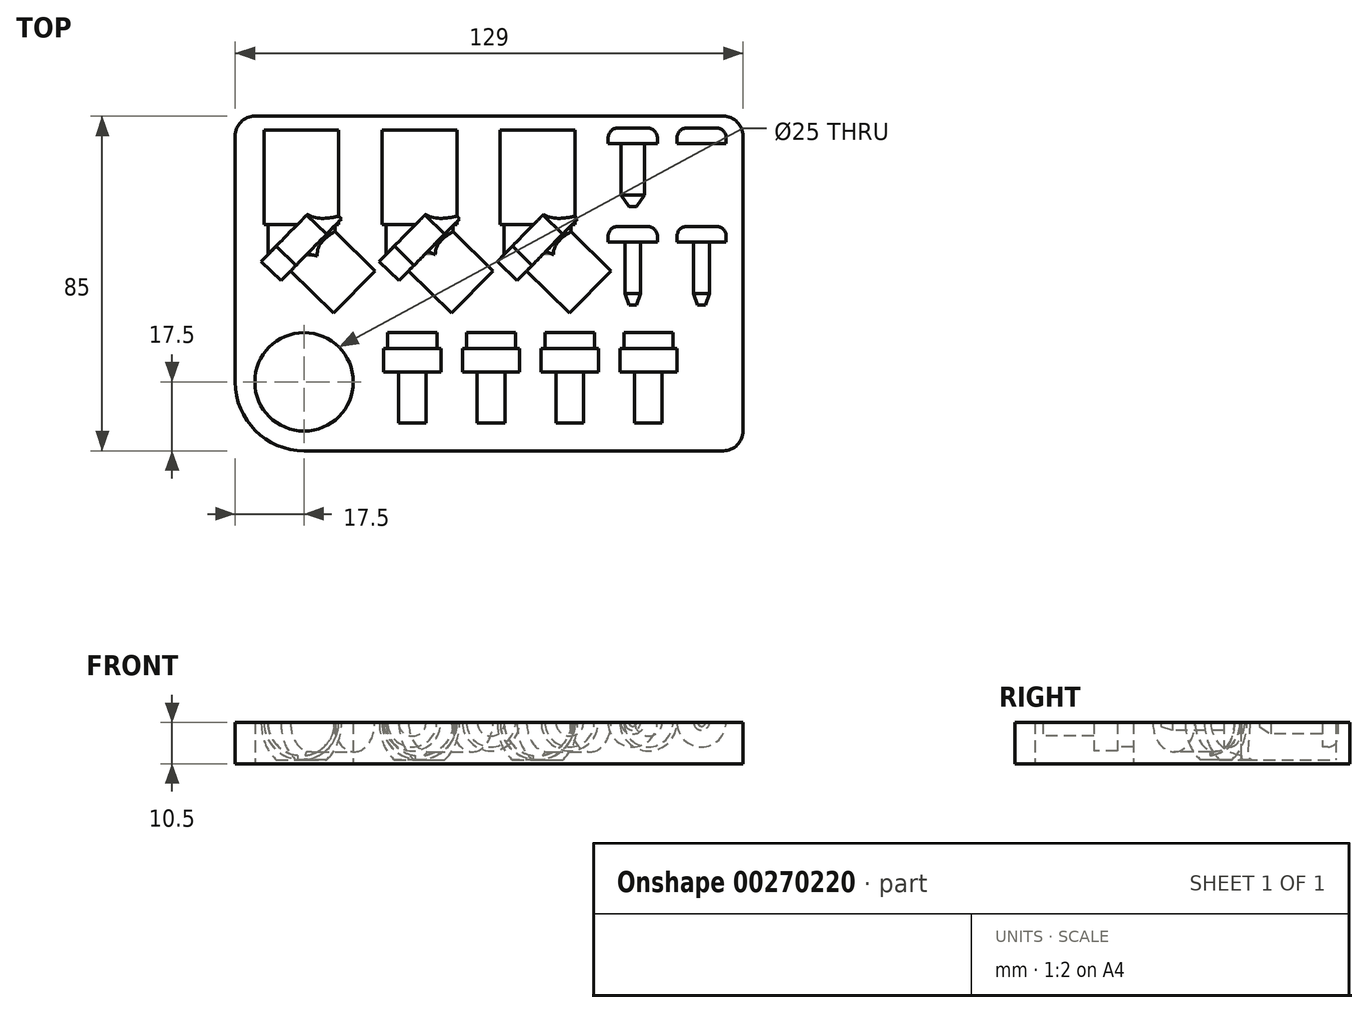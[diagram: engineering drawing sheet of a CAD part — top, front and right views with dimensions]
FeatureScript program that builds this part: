
annotation { "Feature Type Name" : "Feature", "Feature Type Description" : "" }
export const myFeature = defineFeature(function(context is Context, id is Id, definition is map)
    precondition{}
    {
        {
            var Q0;
            Q0=qCreatedBy(makeId("Top.planeOp"),FACE);
            var sketch = newSketch(context, id + "F0", { "sketchPlane" : qUnion([Q0])});
            skLineSegment(sketch, "E0.bottom", {"start": v(17.5, 0) * mm, "end": v(124, 0) * mm});
            skLineSegment(sketch, "E0.top", {"start": v(5, 85) * mm, "end": v(124, 85) * mm});
            skLineSegment(sketch, "E0.left", {"start": v(0, 17.5) * mm, "end": v(0, 80) * mm});
            skLineSegment(sketch, "E0.right", {"start": v(129, 5) * mm, "end": v(129, 80) * mm});
            skLineSegment(sketch, "E1.bottom", {"start": v(17.5, 0) * mm, "end": v(17.5, 0) * mm});
            skLineSegment(sketch, "E1.top", {"start": v(0, 17.5) * mm, "end": v(17.5, 17.5) * mm, "construction": true});
            skLineSegment(sketch, "E1.left", {"start": v(0, 17.5) * mm, "end": v(0, 17.5) * mm});
            skLineSegment(sketch, "E1.right", {"start": v(17.5, 0) * mm, "end": v(17.5, 17.5) * mm, "construction": true});
            skCircle(sketch, "E2", {"center": v(17.5, 17.5) * mm, "radius": 12.5 * mm});
            skPoint(sketch, "E3.visualSharp", {"position": v(0, 0) * mm});
            skArc(sketch, "E3.filletArc", {"start": v(0, 17.5) * mm, "mid": v(5.13, 5.13) * mm, "end": v(17.5, 0) * mm});
            skPoint(sketch, "E4.visualSharp", {"position": v(0, 85) * mm});
            skArc(sketch, "E4.filletArc", {"start": v(5, 85) * mm, "mid": v(1.46, 83.54) * mm, "end": v(0, 80) * mm});
            skPoint(sketch, "E5.visualSharp", {"position": v(129, 85) * mm});
            skArc(sketch, "E5.filletArc", {"start": v(129, 80) * mm, "mid": v(127.54, 83.54) * mm, "end": v(124, 85) * mm});
            skPoint(sketch, "E6.visualSharp", {"position": v(129, 0) * mm});
            skArc(sketch, "E6.filletArc", {"start": v(124, 0) * mm, "mid": v(127.54, 1.46) * mm, "end": v(129, 5) * mm});
            skSolve(sketch);
        }
        {
            var Q0;
            Q0=makeQuery(id+"F0.imprint","IMPRINT",FACE,{"disambiguationData":[TD([[makeQuery(id+"F0.imprint","IMPRINT",EDGE,{"derivedFrom":sQuery(id+"F0.wireOp",EDGE,"E0.bottom")}),1.0]])]});
            extrude(context, id + "F1", {"entities" : qUnion([Q0]), "depth" : 10.5 * mm});
        }
        {
            var Q0;
            Q0=makeQuery(id+"F1.opExtrude","CAP_FACE",FACE,{"disambiguationData":[OSD([sQuery(id+"F0.wireOp",EDGE,"E0.bottom"),sQuery(id+"F0.wireOp",EDGE,"E0.top"),sQuery(id+"F0.wireOp",EDGE,"E0.left"),sQuery(id+"F0.wireOp",EDGE,"E0.right"),sQuery(id+"F0.wireOp",EDGE,"E2"),sQuery(id+"F0.wireOp",EDGE,"E3.filletArc"),sQuery(id+"F0.wireOp",EDGE,"E4.filletArc"),sQuery(id+"F0.wireOp",EDGE,"E5.filletArc"),sQuery(id+"F0.wireOp",EDGE,"E6.filletArc")])],"isStart":false});
            var sketch = newSketch(context, id + "F2", { "sketchPlane" : qUnion([Q0])});
            skLineSegment(sketch, "E7.bottom", {"start": v(0, 0) * mm, "end": v(25, 0) * mm, "construction": true});
            skLineSegment(sketch, "E7.top", {"start": v(0, 35) * mm, "end": v(25, 35) * mm, "construction": true});
            skLineSegment(sketch, "E7.left", {"start": v(0, 0) * mm, "end": v(0, 35) * mm, "construction": true});
            skLineSegment(sketch, "E7.right", {"start": v(25, 0) * mm, "end": v(25, 35) * mm, "construction": true});
            skLineSegment(sketch, "E8", {"start": v(25, 35) * mm, "end": v(14.07, 45.7) * mm});
            skLineSegment(sketch, "E9", {"start": v(14.07, 45.7) * mm, "end": v(11.62, 43.2) * mm});
            skLineSegment(sketch, "E10", {"start": v(11.62, 43.2) * mm, "end": v(6.62, 48.1) * mm});
            skLineSegment(sketch, "E11", {"start": v(6.62, 48.1) * mm, "end": v(14.32, 55.96) * mm});
            skLineSegment(sketch, "E12", {"start": v(14.32, 55.96) * mm, "end": v(30.25, 40.36) * mm});
            skLineSegment(sketch, "E13", {"start": v(25, 35) * mm, "end": v(30.25, 40.36) * mm});
            skLineSegment(sketch, "E14", {"start": v(14.32, 55.96) * mm, "end": v(16.82, 53.51) * mm, "construction": true});
            skLineSegment(sketch, "E15", {"start": v(16.82, 53.51) * mm, "end": v(16.82, 81.51) * mm});
            skLineSegment(sketch, "E16", {"start": v(16.82, 81.51) * mm, "end": v(7.32, 81.51) * mm});
            skLineSegment(sketch, "E17", {"start": v(7.32, 81.51) * mm, "end": v(7.32, 57.51) * mm});
            skLineSegment(sketch, "E18", {"start": v(7.32, 57.51) * mm, "end": v(8.32, 57.51) * mm});
            skLineSegment(sketch, "E19", {"start": v(8.32, 57.51) * mm, "end": v(8.32, 53.16) * mm});
            skLineSegment(sketch, "E20", {"start": v(46.82, 53.51) * mm, "end": v(46.82, 81.51) * mm});
            skLineSegment(sketch, "E21", {"start": v(46.82, 81.51) * mm, "end": v(37.32, 81.51) * mm});
            skLineSegment(sketch, "E22", {"start": v(37.32, 81.51) * mm, "end": v(37.32, 57.51) * mm});
            skLineSegment(sketch, "E23", {"start": v(37.32, 57.51) * mm, "end": v(38.32, 57.51) * mm});
            skLineSegment(sketch, "E24", {"start": v(76.82, 53.51) * mm, "end": v(76.82, 81.51) * mm});
            skLineSegment(sketch, "E25", {"start": v(76.82, 81.51) * mm, "end": v(67.32, 81.51) * mm});
            skLineSegment(sketch, "E26", {"start": v(67.32, 81.51) * mm, "end": v(67.32, 57.51) * mm});
            skLineSegment(sketch, "E27", {"start": v(67.32, 57.51) * mm, "end": v(68.32, 57.51) * mm});
            skLineSegment(sketch, "E28", {"start": v(8.32, 57.51) * mm, "end": v(8.32, 49.51) * mm});
            skLineSegment(sketch, "E29", {"start": v(8.32, 49.51) * mm, "end": v(16.82, 53.51) * mm});
            skLineSegment(sketch, "E30", {"start": v(38.32, 57.51) * mm, "end": v(38.32, 49.51) * mm});
            skLineSegment(sketch, "E31", {"start": v(38.32, 49.51) * mm, "end": v(46.82, 53.51) * mm});
            skLineSegment(sketch, "E32", {"start": v(68.32, 57.51) * mm, "end": v(68.32, 49.51) * mm});
            skLineSegment(sketch, "E33", {"start": v(68.32, 49.51) * mm, "end": v(76.82, 53.51) * mm});
            skLineSegment(sketch, "E34", {"start": v(46.82, 53.51) * mm, "end": v(44.32, 55.96) * mm});
            skLineSegment(sketch, "E35", {"start": v(44.32, 55.96) * mm, "end": v(36.62, 48.1) * mm});
            skLineSegment(sketch, "E36", {"start": v(36.62, 48.1) * mm, "end": v(41.62, 43.2) * mm});
            skLineSegment(sketch, "E37", {"start": v(41.62, 43.2) * mm, "end": v(44.07, 45.7) * mm});
            skLineSegment(sketch, "E38", {"start": v(44.07, 45.7) * mm, "end": v(55, 35) * mm});
            skLineSegment(sketch, "E39", {"start": v(55, 35) * mm, "end": v(60.25, 40.36) * mm});
            skLineSegment(sketch, "E40", {"start": v(46.82, 53.51) * mm, "end": v(60.25, 40.36) * mm});
            skLineSegment(sketch, "E41", {"start": v(76.82, 53.51) * mm, "end": v(74.32, 55.96) * mm});
            skLineSegment(sketch, "E42", {"start": v(74.32, 55.96) * mm, "end": v(66.62, 48.1) * mm});
            skLineSegment(sketch, "E43", {"start": v(66.62, 48.1) * mm, "end": v(71.62, 43.2) * mm});
            skLineSegment(sketch, "E44", {"start": v(71.62, 43.2) * mm, "end": v(74.07, 45.7) * mm});
            skLineSegment(sketch, "E45", {"start": v(74.07, 45.7) * mm, "end": v(85, 35) * mm});
            skLineSegment(sketch, "E46", {"start": v(76.82, 53.51) * mm, "end": v(90.25, 40.36) * mm});
            skLineSegment(sketch, "E47", {"start": v(85, 35) * mm, "end": v(90.25, 40.36) * mm});
            skLineSegment(sketch, "E48", {"start": v(16.82, 53.51) * mm, "end": v(46.82, 53.51) * mm, "construction": true});
            skLineSegment(sketch, "E49", {"start": v(46.82, 53.51) * mm, "end": v(76.82, 53.51) * mm, "construction": true});
            skSolve(sketch);
        }
        {
            var Q0;
            {var subQ0=sQuery(id+"F2.wireOp",EDGE,"E15");Q0=makeQuery(id+"F2.imprint","IMPRINT",FACE,{"disambiguationData":[TD([[makeQuery(id+"F2.imprint","IMPRINT",EDGE,{"derivedFrom":subQ0}),1.0]])]});}
            var Q1;
            {var subQ5=sQuery(id+"F2.wireOp",EDGE,"E29");Q1=makeQuery(id+"F2.imprint","IMPRINT",FACE,{"disambiguationData":[TD([[makeQuery(id+"F2.imprint","IMPRINT",EDGE,{"derivedFrom":subQ5}),1.0]])]});}
            var Q2;
            Q2=sQuery(id+"F2.wireOp",EDGE,"E15");
            revolve(context, id + "F3", {"operationType" : NewBodyOperationType.REMOVE, "entities" : qUnion([Q0, Q1]), "axis" : qUnion([Q2]), "revolveType" : RevolveType.FULL, "oppositeDirection" : true});
        }
        {
            var Q0;
            Q0=makeQuery(id+"F2.imprint","IMPRINT",FACE,{"disambiguationData":[TD([[makeQuery(id+"F2.imprint","IMPRINT",EDGE,{"derivedFrom":sQuery(id+"F2.wireOp",EDGE,"E20")}),1.0]])]});
            var Q1;
            Q1=sQuery(id+"F2.wireOp",EDGE,"E20");
            revolve(context, id + "F4", {"operationType" : NewBodyOperationType.REMOVE, "entities" : qUnion([Q0]), "axis" : qUnion([Q1]), "revolveType" : RevolveType.FULL, "oppositeDirection" : true});
        }
        {
            var Q0;
            Q0=makeQuery(id+"F2.imprint","IMPRINT",FACE,{"disambiguationData":[TD([[makeQuery(id+"F2.imprint","IMPRINT",EDGE,{"derivedFrom":sQuery(id+"F2.wireOp",EDGE,"E24")}),1.0]])]});
            var Q1;
            Q1=sQuery(id+"F2.wireOp",EDGE,"E24");
            revolve(context, id + "F5", {"operationType" : NewBodyOperationType.REMOVE, "entities" : qUnion([Q0]), "axis" : qUnion([Q1]), "revolveType" : RevolveType.FULL, "oppositeDirection" : true});
        }
        {
            var Q0;
            Q0=makeQuery(id+"F2.imprint","IMPRINT",FACE,{"disambiguationData":[TD([[makeQuery(id+"F2.imprint","IMPRINT",EDGE,{"derivedFrom":sQuery(id+"F2.wireOp",EDGE,"E8")}),-1.0]])]});
            var Q1;
            {var subQ5=sQuery(id+"F2.wireOp",EDGE,"E29");Q1=makeQuery(id+"F2.imprint","IMPRINT",FACE,{"disambiguationData":[TD([[makeQuery(id+"F2.imprint","IMPRINT",EDGE,{"derivedFrom":subQ5}),1.0]])]});}
            var Q2;
            Q2=sQuery(id+"F2.wireOp",EDGE,"E12");
            revolve(context, id + "F6", {"operationType" : NewBodyOperationType.REMOVE, "entities" : qUnion([Q0, Q1]), "axis" : qUnion([Q2]), "revolveType" : RevolveType.FULL, "oppositeDirection" : true});
        }
        {
            var Q0;
            {var subQ4=sQuery(id+"F2.wireOp",EDGE,"E31");Q0=makeQuery(id+"F2.imprint","IMPRINT",FACE,{"disambiguationData":[TD([[makeQuery(id+"F2.imprint","IMPRINT",EDGE,{"derivedFrom":subQ4}),-1.0]])]});}
            var Q1;
            {var subQ0=sQuery(id+"F2.wireOp",EDGE,"E31");Q1=makeQuery(id+"F2.imprint","IMPRINT",FACE,{"disambiguationData":[TD([[makeQuery(id+"F2.imprint","IMPRINT",EDGE,{"derivedFrom":subQ0}),1.0]])]});}
            var Q2;
            Q2=sQuery(id+"F2.wireOp",EDGE,"E40");
            revolve(context, id + "F7", {"operationType" : NewBodyOperationType.REMOVE, "entities" : qUnion([Q0, Q1]), "axis" : qUnion([Q2]), "revolveType" : RevolveType.FULL, "oppositeDirection" : true});
        }
        {
            var Q0;
            {var subQ4=sQuery(id+"F2.wireOp",EDGE,"E33");Q0=makeQuery(id+"F2.imprint","IMPRINT",FACE,{"disambiguationData":[TD([[makeQuery(id+"F2.imprint","IMPRINT",EDGE,{"derivedFrom":subQ4}),-1.0]])]});}
            var Q1;
            {var subQ0=sQuery(id+"F2.wireOp",EDGE,"E33");Q1=makeQuery(id+"F2.imprint","IMPRINT",FACE,{"disambiguationData":[TD([[makeQuery(id+"F2.imprint","IMPRINT",EDGE,{"derivedFrom":subQ0}),1.0]])]});}
            var Q2;
            Q2=sQuery(id+"F2.wireOp",EDGE,"E46");
            revolve(context, id + "F8", {"operationType" : NewBodyOperationType.REMOVE, "entities" : qUnion([Q0, Q1]), "axis" : qUnion([Q2]), "revolveType" : RevolveType.FULL, "oppositeDirection" : true});
        }
        {
            var Q0;
            Q0=makeQuery(id+"F1.opExtrude","CAP_FACE",FACE,{"disambiguationData":[OSD([sQuery(id+"F0.wireOp",EDGE,"E0.bottom"),sQuery(id+"F0.wireOp",EDGE,"E0.top"),sQuery(id+"F0.wireOp",EDGE,"E0.left"),sQuery(id+"F0.wireOp",EDGE,"E0.right"),sQuery(id+"F0.wireOp",EDGE,"E2"),sQuery(id+"F0.wireOp",EDGE,"E3.filletArc"),sQuery(id+"F0.wireOp",EDGE,"E4.filletArc"),sQuery(id+"F0.wireOp",EDGE,"E5.filletArc"),sQuery(id+"F0.wireOp",EDGE,"E6.filletArc")])],"isStart":false});
            var sketch = newSketch(context, id + "F9", { "sketchPlane" : qUnion([Q0])});
            skLineSegment(sketch, "E50.0.0", {"start": v(124, 85) * mm, "end": v(5, 85) * mm});
            skArc(sketch, "E50.0.1", {"start": v(5, 85) * mm, "mid": v(1.46, 83.54) * mm, "end": v(0, 80) * mm});
            skLineSegment(sketch, "E50.0.2", {"start": v(0, 80) * mm, "end": v(0, 17.5) * mm});
            skArc(sketch, "E50.0.3", {"start": v(0, 17.5) * mm, "mid": v(5.13, 5.13) * mm, "end": v(17.5, 0) * mm});
            skLineSegment(sketch, "E50.0.4", {"start": v(17.5, 0) * mm, "end": v(124, 0) * mm});
            skArc(sketch, "E50.0.5", {"start": v(124, 0) * mm, "mid": v(127.54, 1.46) * mm, "end": v(129, 5) * mm});
            skLineSegment(sketch, "E50.0.6", {"start": v(129, 5) * mm, "end": v(129, 80) * mm});
            skArc(sketch, "E50.0.7", {"start": v(129, 80) * mm, "mid": v(127.54, 83.54) * mm, "end": v(124, 85) * mm});
            skCircle(sketch, "E51.0", {"center": v(17.5, 17.5) * mm, "radius": 12.5 * mm});
            skSolve(sketch);
        }
        {
            var Q0;
            Q0 = qSketchRegion(id + "F9", true);
            extrude(context, id + "F10", {"entities" : qUnion([Q0]), "operationType" : NewBodyOperationType.ADD, "oppositeDirection" : true, "depth" : 10.5 * mm, "hasSecondDirection" : true, "secondDirectionOppositeDirection" : true, "secondDirectionDepth" : 9.5 * mm});
        }
        {
            var Q0;
            Q0=makeQuery(id+"F1.opExtrude","CAP_FACE",FACE,{"disambiguationData":[OSD([sQuery(id+"F0.wireOp",EDGE,"E0.bottom"),sQuery(id+"F0.wireOp",EDGE,"E0.top"),sQuery(id+"F0.wireOp",EDGE,"E0.left"),sQuery(id+"F0.wireOp",EDGE,"E0.right"),sQuery(id+"F0.wireOp",EDGE,"E2"),sQuery(id+"F0.wireOp",EDGE,"E3.filletArc"),sQuery(id+"F0.wireOp",EDGE,"E4.filletArc"),sQuery(id+"F0.wireOp",EDGE,"E5.filletArc"),sQuery(id+"F0.wireOp",EDGE,"E6.filletArc")])],"isStart":false});
            var sketch = newSketch(context, id + "F11", { "sketchPlane" : qUnion([Q0])});
            skLineSegment(sketch, "E52.bottom", {"start": v(0, 0) * mm, "end": v(101, 0) * mm, "construction": true});
            skLineSegment(sketch, "E52.top", {"start": v(0, 82) * mm, "end": v(101, 82) * mm, "construction": true});
            skLineSegment(sketch, "E52.left", {"start": v(0, 0) * mm, "end": v(0, 82) * mm, "construction": true});
            skLineSegment(sketch, "E52.right", {"start": v(101, 0) * mm, "end": v(101, 82) * mm, "construction": true});
            skLineSegment(sketch, "E53.bottom", {"start": v(101, 82) * mm, "end": v(104.75, 82) * mm});
            skLineSegment(sketch, "E53.top", {"start": v(104, 78) * mm, "end": v(107.25, 78) * mm});
            skLineSegment(sketch, "E53.left", {"start": v(101, 82) * mm, "end": v(101, 78) * mm});
            skLineSegment(sketch, "E53.right", {"start": v(107.25, 79.5) * mm, "end": v(107.25, 78) * mm});
            skPoint(sketch, "E54.visualSharp", {"position": v(107.25, 82) * mm});
            skArc(sketch, "E54.filletArc", {"start": v(107.25, 79.5) * mm, "mid": v(106.52, 81.27) * mm, "end": v(104.75, 82) * mm});
            skLineSegment(sketch, "E55.left", {"start": v(101, 78) * mm, "end": v(101, 72) * mm});
            skLineSegment(sketch, "E55.right", {"start": v(104, 78) * mm, "end": v(104, 65) * mm});
            skLineSegment(sketch, "E56", {"start": v(101, 82) * mm, "end": v(118.5, 82) * mm, "construction": true});
            skLineSegment(sketch, "E57.bottom", {"start": v(118.5, 82) * mm, "end": v(122.25, 82) * mm});
            skLineSegment(sketch, "E57.top", {"start": v(118.5, 78) * mm, "end": v(124.75, 78) * mm});
            skLineSegment(sketch, "E57.left", {"start": v(118.5, 82) * mm, "end": v(118.5, 78) * mm});
            skLineSegment(sketch, "E57.right", {"start": v(124.75, 79.5) * mm, "end": v(124.75, 78) * mm});
            skLineSegment(sketch, "E58.bottom", {"start": v(118.5, 78) * mm, "end": v(121.5, 78) * mm});
            skLineSegment(sketch, "E58.top", {"start": v(118.5, 62) * mm, "end": v(119.5, 62) * mm});
            skLineSegment(sketch, "E58.left", {"start": v(118.5, 78) * mm, "end": v(118.5, 62) * mm});
            skLineSegment(sketch, "E58.right", {"start": v(121.5, 78) * mm, "end": v(121.5, 65) * mm});
            skPoint(sketch, "E59.visualSharp", {"position": v(124.75, 82) * mm});
            skArc(sketch, "E59.filletArc", {"start": v(124.75, 79.5) * mm, "mid": v(124.02, 81.27) * mm, "end": v(122.25, 82) * mm});
            skLineSegment(sketch, "E60", {"start": v(118.5, 62) * mm, "end": v(119.5, 62) * mm, "construction": true});
            skLineSegment(sketch, "E61", {"start": v(119.5, 62) * mm, "end": v(121.5, 65) * mm});
            skLineSegment(sketch, "E62", {"start": v(101, 78) * mm, "end": v(101, 62) * mm});
            skLineSegment(sketch, "E63", {"start": v(101, 62) * mm, "end": v(102, 62) * mm});
            skLineSegment(sketch, "E64", {"start": v(102, 62) * mm, "end": v(104, 65) * mm});
            skLineSegment(sketch, "E65", {"start": v(101, 62) * mm, "end": v(101, 57) * mm, "construction": true});
            skLineSegment(sketch, "E66.bottom", {"start": v(101, 57) * mm, "end": v(104.75, 57) * mm});
            skLineSegment(sketch, "E66.top", {"start": v(103, 53) * mm, "end": v(107.25, 53) * mm});
            skLineSegment(sketch, "E66.left", {"start": v(101, 57) * mm, "end": v(101, 53) * mm});
            skLineSegment(sketch, "E66.right", {"start": v(107.25, 54.5) * mm, "end": v(107.25, 53) * mm});
            skLineSegment(sketch, "E67.left", {"start": v(101, 53) * mm, "end": v(101, 37) * mm});
            skLineSegment(sketch, "E68", {"start": v(103, 53) * mm, "end": v(103, 40) * mm});
            skLineSegment(sketch, "E69", {"start": v(101, 37) * mm, "end": v(102, 37) * mm});
            skLineSegment(sketch, "E70", {"start": v(102, 37) * mm, "end": v(103, 40) * mm});
            skPoint(sketch, "E71.visualSharp", {"position": v(107.25, 57) * mm});
            skArc(sketch, "E71.filletArc", {"start": v(107.25, 54.5) * mm, "mid": v(106.52, 56.27) * mm, "end": v(104.75, 57) * mm});
            skLineSegment(sketch, "E72", {"start": v(101, 57) * mm, "end": v(118.5, 57) * mm, "construction": true});
            skLineSegment(sketch, "E73.bottom", {"start": v(118.5, 57) * mm, "end": v(122.25, 57) * mm});
            skLineSegment(sketch, "E73.top", {"start": v(120.5, 53) * mm, "end": v(124.75, 53) * mm});
            skLineSegment(sketch, "E73.left", {"start": v(118.5, 57) * mm, "end": v(118.5, 53) * mm});
            skLineSegment(sketch, "E73.right", {"start": v(124.75, 54.5) * mm, "end": v(124.75, 53) * mm});
            skLineSegment(sketch, "E74.left", {"start": v(118.5, 53) * mm, "end": v(118.5, 37) * mm});
            skLineSegment(sketch, "E75", {"start": v(120.5, 53) * mm, "end": v(120.5, 40) * mm});
            skLineSegment(sketch, "E76", {"start": v(118.5, 37) * mm, "end": v(119.5, 37) * mm});
            skLineSegment(sketch, "E77", {"start": v(119.5, 37) * mm, "end": v(120.5, 40) * mm});
            skPoint(sketch, "E78.visualSharp", {"position": v(124.75, 57) * mm});
            skArc(sketch, "E78.filletArc", {"start": v(124.75, 54.5) * mm, "mid": v(124.02, 56.27) * mm, "end": v(122.25, 57) * mm});
            skSolve(sketch);
        }
        {
            var Q0;
            Q0=makeQuery(id+"F11.imprint","IMPRINT",FACE,{"disambiguationData":[TD([[makeQuery(id+"F11.imprint","IMPRINT",EDGE,{"derivedFrom":sQuery(id+"F11.wireOp",EDGE,"E53.bottom")}),-1.0]])]});
            var Q1;
            Q1=makeQuery(id+"F11.imprint","IMPRINT",FACE,{"disambiguationData":[TD([[makeQuery(id+"F11.imprint","IMPRINT",EDGE,{"derivedFrom":sQuery(id+"F11.wireOp",EDGE,"E66.bottom")}),-1.0]])]});
            var Q2;
            Q2=sQuery(id+"F11.wireOp",EDGE,"E67.left");
            revolve(context, id + "F12", {"operationType" : NewBodyOperationType.REMOVE, "entities" : qUnion([Q0, Q1]), "axis" : qUnion([Q2]), "revolveType" : RevolveType.FULL, "oppositeDirection" : true});
        }
        {
            var Q0;
            Q0=makeQuery(id+"F11.imprint","IMPRINT",FACE,{"disambiguationData":[TD([[makeQuery(id+"F11.imprint","IMPRINT",EDGE,{"derivedFrom":sQuery(id+"F11.wireOp",EDGE,"E58.bottom")}),-1.0]])]});
            var Q1;
            Q1=makeQuery(id+"F11.imprint","IMPRINT",FACE,{"disambiguationData":[TD([[makeQuery(id+"F11.imprint","IMPRINT",EDGE,{"derivedFrom":sQuery(id+"F11.wireOp",EDGE,"E57.bottom")}),-1.0]])]});
            var Q2;
            Q2=makeQuery(id+"F11.imprint","IMPRINT",FACE,{"disambiguationData":[TD([[makeQuery(id+"F11.imprint","IMPRINT",EDGE,{"derivedFrom":sQuery(id+"F11.wireOp",EDGE,"E73.bottom")}),-1.0]])]});
            var Q3;
            Q3=sQuery(id+"F11.wireOp",EDGE,"E74.left");
            revolve(context, id + "F13", {"operationType" : NewBodyOperationType.REMOVE, "entities" : qUnion([Q0, Q1, Q2]), "axis" : qUnion([Q3]), "revolveType" : RevolveType.FULL, "oppositeDirection" : true});
        }
        {
            var Q0;
            Q0=makeQuery(id+"F1.opExtrude","CAP_FACE",FACE,{"disambiguationData":[OSD([sQuery(id+"F0.wireOp",EDGE,"E0.bottom"),sQuery(id+"F0.wireOp",EDGE,"E0.top"),sQuery(id+"F0.wireOp",EDGE,"E0.left"),sQuery(id+"F0.wireOp",EDGE,"E0.right"),sQuery(id+"F0.wireOp",EDGE,"E2"),sQuery(id+"F0.wireOp",EDGE,"E3.filletArc"),sQuery(id+"F0.wireOp",EDGE,"E4.filletArc"),sQuery(id+"F0.wireOp",EDGE,"E5.filletArc"),sQuery(id+"F0.wireOp",EDGE,"E6.filletArc")])],"isStart":false});
            var sketch = newSketch(context, id + "F14", { "sketchPlane" : qUnion([Q0])});
            skLineSegment(sketch, "E79.bottom", {"start": v(0, 0) * mm, "end": v(45, 0) * mm, "construction": true});
            skLineSegment(sketch, "E79.top", {"start": v(0, 30) * mm, "end": v(45, 30) * mm, "construction": true});
            skLineSegment(sketch, "E79.left", {"start": v(0, 0) * mm, "end": v(0, 30) * mm, "construction": true});
            skLineSegment(sketch, "E79.right", {"start": v(45, 0) * mm, "end": v(45, 17.5) * mm, "construction": true});
            skLineSegment(sketch, "E80.bottom", {"start": v(45, 30) * mm, "end": v(51.25, 30) * mm});
            skLineSegment(sketch, "E80.left", {"start": v(45, 30) * mm, "end": v(45, 26) * mm});
            skLineSegment(sketch, "E80.right", {"start": v(51.25, 30) * mm, "end": v(51.25, 26) * mm});
            skLineSegment(sketch, "E81.bottom", {"start": v(51.25, 26) * mm, "end": v(52.25, 26) * mm});
            skLineSegment(sketch, "E81.left", {"start": v(45, 26) * mm, "end": v(45, 17.5) * mm});
            skPoint(sketch, "E81.right.end.orphan", {"position": v(47.25, 17.5) * mm});
            skLineSegment(sketch, "E82.trimOffspring", {"start": v(45, 26) * mm, "end": v(45, 30) * mm, "construction": true});
            skLineSegment(sketch, "E83", {"start": v(52.25, 26) * mm, "end": v(52.25, 20) * mm});
            skLineSegment(sketch, "E84", {"start": v(52.25, 20) * mm, "end": v(48.5, 20) * mm});
            skLineSegment(sketch, "E85", {"start": v(45, 20) * mm, "end": v(45, 26) * mm});
            skLineSegment(sketch, "E86.top", {"start": v(45, 7) * mm, "end": v(48.5, 7) * mm});
            skLineSegment(sketch, "E86.left", {"start": v(45, 20) * mm, "end": v(45, 7) * mm});
            skLineSegment(sketch, "E86.right", {"start": v(48.5, 20) * mm, "end": v(48.5, 7) * mm});
            skLineSegment(sketch, "E87", {"start": v(45, 30) * mm, "end": v(65, 30) * mm, "construction": true});
            skLineSegment(sketch, "E88", {"start": v(65, 30) * mm, "end": v(85, 30) * mm, "construction": true});
            skLineSegment(sketch, "E89", {"start": v(85, 30) * mm, "end": v(105, 30) * mm, "construction": true});
            skLineSegment(sketch, "E90.bottom", {"start": v(65, 30) * mm, "end": v(71.25, 30) * mm});
            skLineSegment(sketch, "E90.left", {"start": v(65, 30) * mm, "end": v(65, 26) * mm});
            skLineSegment(sketch, "E90.right", {"start": v(71.25, 30) * mm, "end": v(71.25, 26) * mm});
            skLineSegment(sketch, "E91.bottom", {"start": v(85, 30) * mm, "end": v(91.25, 30) * mm});
            skLineSegment(sketch, "E91.left", {"start": v(85, 30) * mm, "end": v(85, 26) * mm});
            skLineSegment(sketch, "E91.right", {"start": v(91.25, 30) * mm, "end": v(91.25, 26) * mm});
            skLineSegment(sketch, "E92.bottom", {"start": v(105, 30) * mm, "end": v(111.25, 30) * mm});
            skLineSegment(sketch, "E92.left", {"start": v(105, 30) * mm, "end": v(105, 26) * mm});
            skLineSegment(sketch, "E92.right", {"start": v(111.25, 30) * mm, "end": v(111.25, 26) * mm});
            skLineSegment(sketch, "E93.bottom", {"start": v(71.25, 26) * mm, "end": v(72.25, 26) * mm});
            skLineSegment(sketch, "E93.top", {"start": v(68.5, 20) * mm, "end": v(72.25, 20) * mm});
            skLineSegment(sketch, "E93.left", {"start": v(65, 26) * mm, "end": v(65, 20) * mm});
            skLineSegment(sketch, "E93.right", {"start": v(72.25, 26) * mm, "end": v(72.25, 20) * mm});
            skLineSegment(sketch, "E94.bottom", {"start": v(91.25, 26) * mm, "end": v(92.25, 26) * mm});
            skLineSegment(sketch, "E94.top", {"start": v(88.5, 20) * mm, "end": v(92.25, 20) * mm});
            skLineSegment(sketch, "E94.left", {"start": v(85, 26) * mm, "end": v(85, 20) * mm});
            skLineSegment(sketch, "E94.right", {"start": v(92.25, 26) * mm, "end": v(92.25, 20) * mm});
            skLineSegment(sketch, "E95.bottom", {"start": v(111.25, 26) * mm, "end": v(112.25, 26) * mm});
            skLineSegment(sketch, "E95.top", {"start": v(108.5, 20) * mm, "end": v(112.25, 20) * mm});
            skLineSegment(sketch, "E95.left", {"start": v(105, 26) * mm, "end": v(105, 20) * mm});
            skLineSegment(sketch, "E95.right", {"start": v(112.25, 26) * mm, "end": v(112.25, 20) * mm});
            skLineSegment(sketch, "E96.top", {"start": v(65, 7) * mm, "end": v(68.5, 7) * mm});
            skLineSegment(sketch, "E96.left", {"start": v(65, 20) * mm, "end": v(65, 7) * mm});
            skLineSegment(sketch, "E96.right", {"start": v(68.5, 20) * mm, "end": v(68.5, 7) * mm});
            skLineSegment(sketch, "E97.top", {"start": v(85, 7) * mm, "end": v(88.5, 7) * mm});
            skLineSegment(sketch, "E97.left", {"start": v(85, 20) * mm, "end": v(85, 7) * mm});
            skLineSegment(sketch, "E97.right", {"start": v(88.5, 20) * mm, "end": v(88.5, 7) * mm});
            skLineSegment(sketch, "E98.top", {"start": v(105, 7) * mm, "end": v(108.5, 7) * mm});
            skLineSegment(sketch, "E98.left", {"start": v(105, 20) * mm, "end": v(105, 7) * mm});
            skLineSegment(sketch, "E98.right", {"start": v(108.5, 20) * mm, "end": v(108.5, 7) * mm});
            skSolve(sketch);
        }
        {
            var Q0;
            Q0=makeQuery(id+"F14.imprint","IMPRINT",FACE,{"disambiguationData":[TD([[makeQuery(id+"F14.imprint","IMPRINT",EDGE,{"derivedFrom":sQuery(id+"F14.wireOp",EDGE,"E80.bottom")}),-1.0]])]});
            var Q1;
            Q1=sQuery(id+"F14.wireOp",EDGE,"E86.left");
            revolve(context, id + "F15", {"operationType" : NewBodyOperationType.REMOVE, "entities" : qUnion([Q0]), "axis" : qUnion([Q1]), "revolveType" : RevolveType.FULL, "oppositeDirection" : true});
        }
        {
            var Q0;
            Q0=makeQuery(id+"F14.imprint","IMPRINT",FACE,{"disambiguationData":[TD([[makeQuery(id+"F14.imprint","IMPRINT",EDGE,{"derivedFrom":sQuery(id+"F14.wireOp",EDGE,"E90.bottom")}),-1.0]])]});
            var Q1;
            Q1=sQuery(id+"F14.wireOp",EDGE,"E96.left");
            revolve(context, id + "F16", {"operationType" : NewBodyOperationType.REMOVE, "entities" : qUnion([Q0]), "axis" : qUnion([Q1]), "revolveType" : RevolveType.FULL, "oppositeDirection" : true});
        }
        {
            var Q0;
            Q0=makeQuery(id+"F14.imprint","IMPRINT",FACE,{"disambiguationData":[TD([[makeQuery(id+"F14.imprint","IMPRINT",EDGE,{"derivedFrom":sQuery(id+"F14.wireOp",EDGE,"E91.bottom")}),-1.0]])]});
            var Q1;
            Q1=sQuery(id+"F14.wireOp",EDGE,"E97.left");
            revolve(context, id + "F17", {"operationType" : NewBodyOperationType.REMOVE, "entities" : qUnion([Q0]), "axis" : qUnion([Q1]), "revolveType" : RevolveType.FULL, "oppositeDirection" : true});
        }
        {
            var Q0;
            Q0=makeQuery(id+"F14.imprint","IMPRINT",FACE,{"disambiguationData":[TD([[makeQuery(id+"F14.imprint","IMPRINT",EDGE,{"derivedFrom":sQuery(id+"F14.wireOp",EDGE,"E92.bottom")}),-1.0]])]});
            var Q1;
            Q1=sQuery(id+"F14.wireOp",EDGE,"E98.left");
            revolve(context, id + "F18", {"operationType" : NewBodyOperationType.REMOVE, "entities" : qUnion([Q0]), "axis" : qUnion([Q1]), "revolveType" : RevolveType.FULL, "oppositeDirection" : true});
        }
    });
